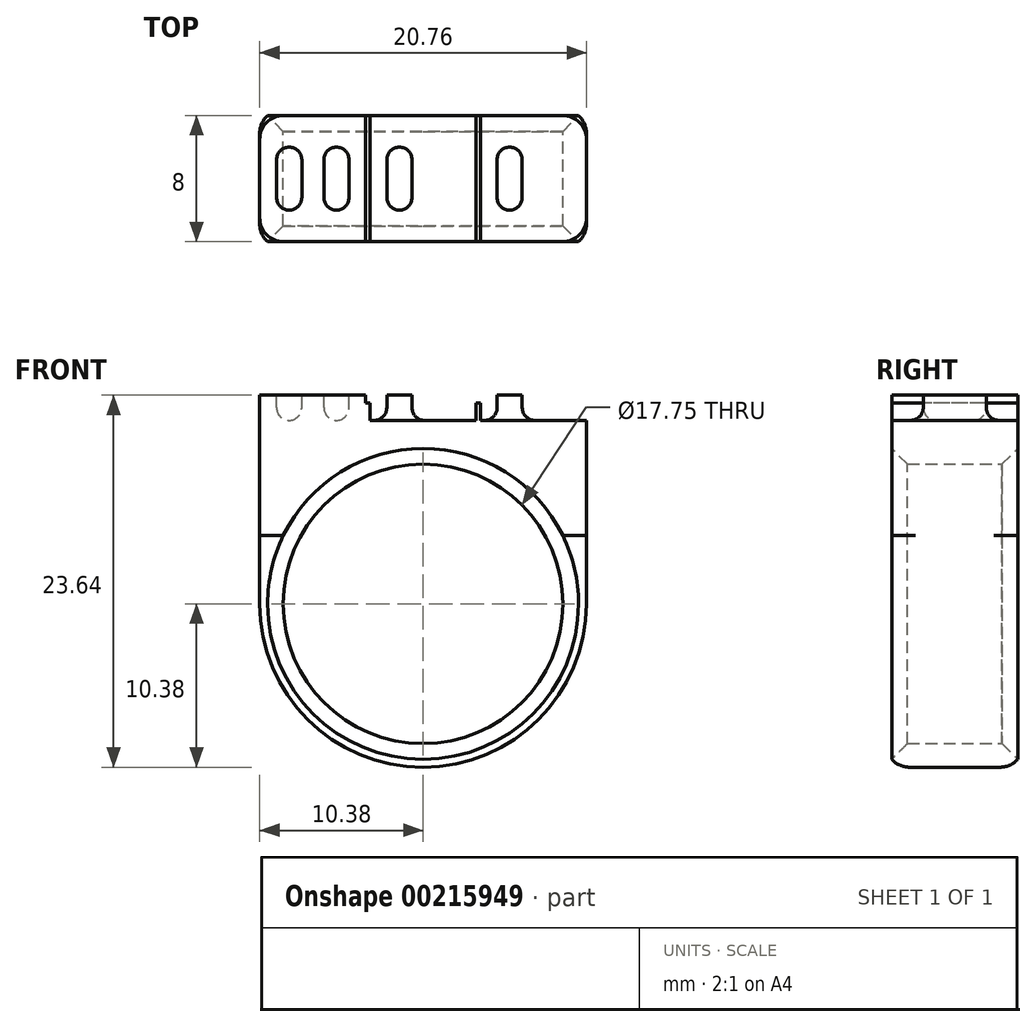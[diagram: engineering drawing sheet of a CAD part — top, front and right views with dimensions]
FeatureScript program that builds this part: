
annotation { "Feature Type Name" : "Feature", "Feature Type Description" : "" }
export const myFeature = defineFeature(function(context is Context, id is Id, definition is map)
    precondition{}
    {
        {
            var Q0;
            Q0=qCreatedBy(makeId("Front.planeOp"),FACE);
            var sketch = newSketch(context, id + "F0", { "sketchPlane" : qUnion([Q0])});
            skCircle(sketch, "E0", {"center": v(0, 0) * mm, "radius": 8.88 * mm});
            skCircle(sketch, "E1.0", {"center": v(0, 0) * mm, "radius": 10.38 * mm});
            skCircle(sketch, "E2.0", {"center": v(0, 0) * mm, "radius": 20.38 * mm});
            skLineSegment(sketch, "E3", {"start": v(10.38, 0) * mm, "end": v(10.38, 17.54) * mm});
            skLineSegment(sketch, "E4.MirrorCS", {"start": v(-10.38, 0) * mm, "end": v(-10.38, 17.54) * mm});
            skCircle(sketch, "E5.0", {"center": v(0, 0) * mm, "radius": 19.38 * mm});
            skLineSegment(sketch, "E6", {"start": v(-10.37, 13.26) * mm, "end": v(10.38, 13.26) * mm});
            skSolve(sketch);
        }
        {
            var Q0;
            Q0=makeQuery(id+"F0.imprint","IMPRINT",FACE,{"disambiguationData":[TD([[makeQuery(id+"F0.imprint","IMPRINT",EDGE,{"derivedFrom":sQuery(id+"F0.wireOp",EDGE,"E0")}),-1.0]])]});
            extrude(context, id + "F1", {"entities" : qUnion([Q0]), "depth" : 4 * mm, "hasSecondDirection" : true, "secondDirectionOppositeDirection" : true, "secondDirectionDepth" : 4 * mm});
        }
        {
            var Q0;
            Q0=makeQuery(id+"F1.opExtrude","CAP_EDGE",EDGE,{"disambiguationData":[OSD([sQuery(id+"F0.wireOp",EDGE,"E0")])],"isStart":false});
            var Q1;
            Q1=makeQuery(id+"F1.opExtrude","CAP_EDGE",EDGE,{"disambiguationData":[OSD([sQuery(id+"F0.wireOp",EDGE,"E0")])],"isStart":true});
            chamfer(context, id + "F2", {"entities" : qUnion([Q0, Q1]), "width" : 1 * mm, "tangentPropagation" : true});
        }
        {
            var Q0;
            {var subQ0=sQuery(id+"F0.wireOp",EDGE,"E3");var subQ1=sQuery(id+"F0.wireOp",EDGE,"E1.0");var subQ2=makeQuery(id+"F0.imprint","INTERSECT",VERTEX,{"derivedFrom":[subQ1,subQ0]});Q0=makeQuery(id+"F0.imprint","IMPRINT",FACE,{"disambiguationData":[TD([[makeQuery(id+"F0.imprint","IMPRINT",EDGE,{"disambiguationData":[TD([[subQ2,-1.0]])],"derivedFrom":subQ1}),-1.0]])]});}
            extrude(context, id + "F3", {"entities" : qUnion([Q0]), "operationType" : NewBodyOperationType.ADD, "depth" : 4 * mm, "hasSecondDirection" : true, "secondDirectionOppositeDirection" : true, "secondDirectionDepth" : 4 * mm});
        }
        {
            var Q0;
            {var subQ0=sQuery(id+"F0.wireOp",EDGE,"E3");var subQ1=sQuery(id+"F0.wireOp",EDGE,"E2.0");var subQ2=makeQuery(id+"F0.imprint","INTERSECT",VERTEX,{"derivedFrom":[subQ1,subQ0]});Q0=makeQuery(id+"F0.imprint","IMPRINT",FACE,{"disambiguationData":[TD([[makeQuery(id+"F0.imprint","IMPRINT",EDGE,{"disambiguationData":[TD([[subQ2,-1.0]])],"derivedFrom":subQ1}),1.0]])]});}
            extrude(context, id + "F4", {"entities" : qUnion([Q0]), "operationType" : NewBodyOperationType.REMOVE, "oppositeDirection" : true, "depth" : .5 * mm, "hasSecondDirection" : true, "secondDirectionOppositeDirection" : false, "secondDirectionDepth" : .5 * mm});
        }
        {
            var Q0;
            Q0=makeQuery(id+"F3.opExtrude","SWEPT_FACE",FACE,{"disambiguationData":[OSD([sQuery(id+"F0.wireOp",EDGE,"E6")])]});
            var sketch = newSketch(context, id + "F5", { "sketchPlane" : qUnion([Q0])});
            skLineSegment(sketch, "E7.bottom", {"start": v(1.5, 2) * mm, "end": v(1.5, 2) * mm});
            skLineSegment(sketch, "E7.top", {"start": v(1.5, -2) * mm, "end": v(1.5, -2) * mm});
            skLineSegment(sketch, "E7.left", {"start": v(0.7, 1.2) * mm, "end": v(0.7, -1.2) * mm});
            skLineSegment(sketch, "E7.right", {"start": v(2.3, 1.2) * mm, "end": v(2.3, -1.2) * mm});
            skLineSegment(sketch, "E8", {"start": v(0.7, 2) * mm, "end": v(2.3, -2) * mm, "construction": true});
            skLineSegment(sketch, "E9", {"start": v(2.3, 2) * mm, "end": v(0.7, -2) * mm, "construction": true});
            skPoint(sketch, "E10", {"position": v(1.5, 0) * mm});
            skPoint(sketch, "E11", {"position": v(3.5, 0) * mm});
            skLineSegment(sketch, "E12", {"start": v(3.5, 4) * mm, "end": v(3.5, 0) * mm, "construction": true});
            skLineSegment(sketch, "E13", {"start": v(3.5, -4) * mm, "end": v(3.5, 0) * mm, "construction": true});
            skPoint(sketch, "E14.visualSharp", {"position": v(0.7, 2) * mm});
            skArc(sketch, "E14.filletArc", {"start": v(1.5, 2) * mm, "mid": v(0.93, 1.77) * mm, "end": v(0.7, 1.2) * mm});
            skPoint(sketch, "E15.visualSharp", {"position": v(2.3, 2) * mm});
            skArc(sketch, "E15.filletArc", {"start": v(2.3, 1.2) * mm, "mid": v(2.07, 1.77) * mm, "end": v(1.5, 2) * mm});
            skPoint(sketch, "E16.visualSharp", {"position": v(2.3, -2) * mm});
            skArc(sketch, "E16.filletArc", {"start": v(1.5, -2) * mm, "mid": v(2.07, -1.77) * mm, "end": v(2.3, -1.2) * mm});
            skPoint(sketch, "E17.visualSharp", {"position": v(0.7, -2) * mm});
            skArc(sketch, "E17.filletArc", {"start": v(0.7, -1.2) * mm, "mid": v(0.93, -1.77) * mm, "end": v(1.5, -2) * mm});
            skPoint(sketch, "E18.MirrorP", {"position": v(4.7, -2) * mm});
            skLineSegment(sketch, "E19.MirrorCS", {"start": v(5.5, -2) * mm, "end": v(5.5, -2) * mm});
            skPoint(sketch, "E20.MirrorP", {"position": v(6.3, 2) * mm});
            skLineSegment(sketch, "E21.MirrorCS", {"start": v(5.5, 2) * mm, "end": v(5.5, 2) * mm});
            skPoint(sketch, "E22.MirrorP", {"position": v(6.3, -2) * mm});
            skArc(sketch, "E23.MirrorCS", {"start": v(6.3, -1.2) * mm, "mid": v(6.07, -1.77) * mm, "end": v(5.5, -2) * mm});
            skArc(sketch, "E24.MirrorCS", {"start": v(5.5, -2) * mm, "mid": v(4.93, -1.77) * mm, "end": v(4.7, -1.2) * mm});
            skPoint(sketch, "E25.MirrorP", {"position": v(5.5, 0) * mm});
            skLineSegment(sketch, "E26.MirrorCS", {"start": v(4.7, 2) * mm, "end": v(6.3, -2) * mm, "construction": true});
            skArc(sketch, "E27.MirrorCS", {"start": v(4.7, 1.2) * mm, "mid": v(4.93, 1.77) * mm, "end": v(5.5, 2) * mm});
            skPoint(sketch, "E28.MirrorP", {"position": v(4.7, 2) * mm});
            skLineSegment(sketch, "E29.MirrorCS", {"start": v(6.3, 2) * mm, "end": v(4.7, -2) * mm, "construction": true});
            skLineSegment(sketch, "E30.MirrorCS", {"start": v(6.3, 1.2) * mm, "end": v(6.3, -1.2) * mm});
            skLineSegment(sketch, "E31.MirrorCS", {"start": v(4.7, 1.2) * mm, "end": v(4.7, -1.2) * mm});
            skArc(sketch, "E32.MirrorCS", {"start": v(5.5, 2) * mm, "mid": v(6.07, 1.77) * mm, "end": v(6.3, 1.2) * mm});
            skPoint(sketch, "E33.MirrorP", {"position": v(-2.3, -2) * mm});
            skLineSegment(sketch, "E34.MirrorCS", {"start": v(-5.5, 2) * mm, "end": v(-5.5, 2) * mm});
            skLineSegment(sketch, "E35.MirrorCS", {"start": v(-4.7, 2) * mm, "end": v(-6.3, -2) * mm, "construction": true});
            skPoint(sketch, "E36.MirrorP", {"position": v(-0.7, -2) * mm});
            skArc(sketch, "E37.MirrorCS", {"start": v(-5.5, -2) * mm, "mid": v(-4.93, -1.77) * mm, "end": v(-4.7, -1.2) * mm});
            skArc(sketch, "E38.MirrorCS", {"start": v(-6.3, -1.2) * mm, "mid": v(-6.07, -1.77) * mm, "end": v(-5.5, -2) * mm});
            skArc(sketch, "E39.MirrorCS", {"start": v(-0.7, -1.2) * mm, "mid": v(-0.93, -1.77) * mm, "end": v(-1.5, -2) * mm});
            skArc(sketch, "E40.MirrorCS", {"start": v(-1.5, -2) * mm, "mid": v(-2.07, -1.77) * mm, "end": v(-2.3, -1.2) * mm});
            skArc(sketch, "E41.MirrorCS", {"start": v(-2.3, 1.2) * mm, "mid": v(-2.07, 1.77) * mm, "end": v(-1.5, 2) * mm});
            skArc(sketch, "E42.MirrorCS", {"start": v(-1.5, 2) * mm, "mid": v(-0.93, 1.77) * mm, "end": v(-0.7, 1.2) * mm});
            skLineSegment(sketch, "E43.MirrorCS", {"start": v(-2.3, 2) * mm, "end": v(-0.7, -2) * mm, "construction": true});
            skLineSegment(sketch, "E44.MirrorCS", {"start": v(-0.7, 2) * mm, "end": v(-2.3, -2) * mm, "construction": true});
            skArc(sketch, "E45.MirrorCS", {"start": v(-5.5, 2) * mm, "mid": v(-6.07, 1.77) * mm, "end": v(-6.3, 1.2) * mm});
            skPoint(sketch, "E46.MirrorP", {"position": v(-2.3, 2) * mm});
            skArc(sketch, "E47.MirrorCS", {"start": v(-4.7, 1.2) * mm, "mid": v(-4.93, 1.77) * mm, "end": v(-5.5, 2) * mm});
            skPoint(sketch, "E48.MirrorP", {"position": v(-0.7, 2) * mm});
            skLineSegment(sketch, "E49.MirrorCS", {"start": v(-2.3, 1.2) * mm, "end": v(-2.3, -1.2) * mm});
            skLineSegment(sketch, "E50.MirrorCS", {"start": v(-1.5, -2) * mm, "end": v(-1.5, -2) * mm});
            skPoint(sketch, "E51.MirrorP", {"position": v(-5.5, 0) * mm});
            skPoint(sketch, "E52.MirrorP", {"position": v(-6.3, 2) * mm});
            skPoint(sketch, "E53.MirrorP", {"position": v(-1.5, 0) * mm});
            skLineSegment(sketch, "E54.MirrorCS", {"start": v(-6.3, 2) * mm, "end": v(-4.7, -2) * mm, "construction": true});
            skLineSegment(sketch, "E55.MirrorCS", {"start": v(-0.7, 1.2) * mm, "end": v(-0.7, -1.2) * mm});
            skPoint(sketch, "E56.MirrorP", {"position": v(-6.3, -2) * mm});
            skPoint(sketch, "E57.MirrorP", {"position": v(-4.7, 2) * mm});
            skLineSegment(sketch, "E58.MirrorCS", {"start": v(-5.5, -2) * mm, "end": v(-5.5, -2) * mm});
            skPoint(sketch, "E59.MirrorP", {"position": v(-3.5, 0) * mm});
            skLineSegment(sketch, "E60.MirrorCS", {"start": v(-1.5, 2) * mm, "end": v(-1.5, 2) * mm});
            skLineSegment(sketch, "E61.MirrorCS", {"start": v(-4.7, 1.2) * mm, "end": v(-4.7, -1.2) * mm});
            skLineSegment(sketch, "E62.MirrorCS", {"start": v(-6.3, 1.2) * mm, "end": v(-6.3, -1.2) * mm});
            skPoint(sketch, "E63.MirrorP", {"position": v(-4.7, -2) * mm});
            skPoint(sketch, "E64", {"position": v(-10.38, 4) * mm});
            skPoint(sketch, "E65", {"position": v(10.38, 4) * mm});
            skPoint(sketch, "E66", {"position": v(7, 0) * mm});
            skLineSegment(sketch, "E67", {"start": v(7, -4) * mm, "end": v(7, 0) * mm, "construction": true});
            skLineSegment(sketch, "E68.MirrorCS", {"start": v(8.5, -2) * mm, "end": v(8.5, -2) * mm});
            skLineSegment(sketch, "E69.MirrorCS", {"start": v(8.5, 2) * mm, "end": v(8.5, 2) * mm});
            skPoint(sketch, "E70.MirrorP", {"position": v(9.3, 2) * mm});
            skPoint(sketch, "E71.MirrorP", {"position": v(9.3, -2) * mm});
            skLineSegment(sketch, "E72.MirrorCS", {"start": v(9.3, 1.2) * mm, "end": v(9.3, -1.2) * mm});
            skPoint(sketch, "E73.MirrorP", {"position": v(8.5, 0) * mm});
            skArc(sketch, "E74.MirrorCS", {"start": v(9.3, 1.2) * mm, "mid": v(9.07, 1.77) * mm, "end": v(8.5, 2) * mm});
            skPoint(sketch, "E75.MirrorP", {"position": v(7.7, 2) * mm});
            skArc(sketch, "E76.MirrorCS", {"start": v(8.5, 2) * mm, "mid": v(7.93, 1.77) * mm, "end": v(7.7, 1.2) * mm});
            skLineSegment(sketch, "E77.MirrorCS", {"start": v(9.3, 2) * mm, "end": v(7.7, -2) * mm, "construction": true});
            skLineSegment(sketch, "E78.MirrorCS", {"start": v(7.7, 1.2) * mm, "end": v(7.7, -1.2) * mm});
            skArc(sketch, "E79.MirrorCS", {"start": v(7.7, -1.2) * mm, "mid": v(7.93, -1.77) * mm, "end": v(8.5, -2) * mm});
            skArc(sketch, "E80.MirrorCS", {"start": v(8.5, -2) * mm, "mid": v(9.07, -1.77) * mm, "end": v(9.3, -1.2) * mm});
            skPoint(sketch, "E81.MirrorP", {"position": v(7.7, -2) * mm});
            skLineSegment(sketch, "E82.MirrorCS", {"start": v(7.7, 2) * mm, "end": v(9.3, -2) * mm, "construction": true});
            skLineSegment(sketch, "E83.MirrorCS", {"start": v(-8.5, 2) * mm, "end": v(-8.5, 2) * mm});
            skLineSegment(sketch, "E84.MirrorCS", {"start": v(-8.5, -2) * mm, "end": v(-8.5, -2) * mm});
            skLineSegment(sketch, "E85.MirrorCS", {"start": v(-9.3, 2) * mm, "end": v(-7.7, -2) * mm, "construction": true});
            skPoint(sketch, "E86.MirrorP", {"position": v(-7.7, 2) * mm});
            skLineSegment(sketch, "E87.MirrorCS", {"start": v(-7.7, 1.2) * mm, "end": v(-7.7, -1.2) * mm});
            skLineSegment(sketch, "E88.MirrorCS", {"start": v(-7.7, 2) * mm, "end": v(-9.3, -2) * mm, "construction": true});
            skLineSegment(sketch, "E89.MirrorCS", {"start": v(-9.3, 1.2) * mm, "end": v(-9.3, -1.2) * mm});
            skPoint(sketch, "E90.MirrorP", {"position": v(-8.5, 0) * mm});
            skArc(sketch, "E91.MirrorCS", {"start": v(-9.3, 1.2) * mm, "mid": v(-9.07, 1.77) * mm, "end": v(-8.5, 2) * mm});
            skArc(sketch, "E92.MirrorCS", {"start": v(-7.7, -1.2) * mm, "mid": v(-7.93, -1.77) * mm, "end": v(-8.5, -2) * mm});
            skArc(sketch, "E93.MirrorCS", {"start": v(-8.5, 2) * mm, "mid": v(-7.93, 1.77) * mm, "end": v(-7.7, 1.2) * mm});
            skPoint(sketch, "E94.MirrorP", {"position": v(-9.3, 2) * mm});
            skArc(sketch, "E95.MirrorCS", {"start": v(-8.5, -2) * mm, "mid": v(-9.07, -1.77) * mm, "end": v(-9.3, -1.2) * mm});
            skPoint(sketch, "E96.MirrorP", {"position": v(-9.3, -2) * mm});
            skPoint(sketch, "E97.MirrorP", {"position": v(-7.7, -2) * mm});
            skLineSegment(sketch, "E98", {"start": v(3.35, 4) * mm, "end": v(3.35, -4) * mm});
            skLineSegment(sketch, "E99.MirrorCS", {"start": v(3.65, 4) * mm, "end": v(3.65, -4) * mm});
            skLineSegment(sketch, "E100", {"start": v(3.35, 4) * mm, "end": v(3.65, 4) * mm});
            skLineSegment(sketch, "E101", {"start": v(3.35, -4) * mm, "end": v(3.65, -4) * mm});
            skLineSegment(sketch, "E102.MirrorCS", {"start": v(-3.35, 4) * mm, "end": v(-3.65, 4) * mm});
            skLineSegment(sketch, "E103.MirrorCS", {"start": v(-3.35, -4) * mm, "end": v(-3.65, -4) * mm});
            skLineSegment(sketch, "E104.MirrorCS", {"start": v(-3.35, 4) * mm, "end": v(-3.35, -4) * mm});
            skLineSegment(sketch, "E105.MirrorCS", {"start": v(-3.65, 4) * mm, "end": v(-3.65, -4) * mm});
            skLineSegment(sketch, "E106.MirrorCS", {"start": v(-3.5, -4) * mm, "end": v(-3.5, 0) * mm, "construction": true});
            skLineSegment(sketch, "E107.MirrorCS", {"start": v(-3.5, 4) * mm, "end": v(-3.5, 0) * mm, "construction": true});
            skSolve(sketch);
        }
        {
            var Q0;
            Q0=makeQuery(id+"F5.imprint","IMPRINT",FACE,{"disambiguationData":[TD([[makeQuery(id+"F5.imprint","IMPRINT",EDGE,{"derivedFrom":sQuery(id+"F5.wireOp",EDGE,"E72.MirrorCS")}),-1.0]])]});
            var Q1;
            Q1=makeQuery(id+"F5.imprint","IMPRINT",FACE,{"disambiguationData":[TD([[makeQuery(id+"F5.imprint","IMPRINT",EDGE,{"derivedFrom":sQuery(id+"F5.wireOp",EDGE,"E23.MirrorCS")}),-1.0]])]});
            var Q2;
            Q2=makeQuery(id+"F5.imprint","IMPRINT",FACE,{"disambiguationData":[TD([[makeQuery(id+"F5.imprint","IMPRINT",EDGE,{"derivedFrom":sQuery(id+"F5.wireOp",EDGE,"E7.left")}),1.0]])]});
            var Q3;
            Q3=makeQuery(id+"F5.imprint","IMPRINT",FACE,{"disambiguationData":[TD([[makeQuery(id+"F5.imprint","IMPRINT",EDGE,{"derivedFrom":sQuery(id+"F5.wireOp",EDGE,"E39.MirrorCS")}),-1.0]])]});
            var Q4;
            Q4=makeQuery(id+"F5.imprint","IMPRINT",FACE,{"disambiguationData":[TD([[makeQuery(id+"F5.imprint","IMPRINT",EDGE,{"derivedFrom":sQuery(id+"F5.wireOp",EDGE,"E37.MirrorCS")}),1.0]])]});
            var Q5;
            Q5=makeQuery(id+"F5.imprint","IMPRINT",FACE,{"disambiguationData":[TD([[makeQuery(id+"F5.imprint","IMPRINT",EDGE,{"derivedFrom":sQuery(id+"F5.wireOp",EDGE,"E87.MirrorCS")}),-1.0]])]});
            extrude(context, id + "F6", {"entities" : qUnion([Q0, Q1, Q2, Q3, Q4, Q5]), "operationType" : NewBodyOperationType.REMOVE, "oppositeDirection" : true, "depth" : 1.6 * mm});
        }
        {
            var Q0;
            Q0=makeQuery(id+"F6.boolean.opBoolean","COPY",EDGE,{"derivedFrom":makeQuery(id+"F6.opExtrude","CAP_EDGE",EDGE,{"disambiguationData":[OSD([sQuery(id+"F5.wireOp",EDGE,"E74.MirrorCS"),sQuery(id+"F5.wireOp",EDGE,"E76.MirrorCS")])],"isStart":false})});
            var Q1;
            Q1=makeQuery(id+"F6.boolean.opBoolean","COPY",EDGE,{"derivedFrom":makeQuery(id+"F6.opExtrude","CAP_EDGE",EDGE,{"disambiguationData":[OSD([sQuery(id+"F5.wireOp",EDGE,"E27.MirrorCS"),sQuery(id+"F5.wireOp",EDGE,"E32.MirrorCS")])],"isStart":false})});
            var Q2;
            Q2=makeQuery(id+"F6.boolean.opBoolean","COPY",EDGE,{"derivedFrom":makeQuery(id+"F6.opExtrude","CAP_EDGE",EDGE,{"disambiguationData":[OSD([sQuery(id+"F5.wireOp",EDGE,"E14.filletArc"),sQuery(id+"F5.wireOp",EDGE,"E15.filletArc")])],"isStart":false})});
            var Q3;
            Q3=makeQuery(id+"F6.boolean.opBoolean","COPY",EDGE,{"derivedFrom":makeQuery(id+"F6.opExtrude","CAP_EDGE",EDGE,{"disambiguationData":[OSD([sQuery(id+"F5.wireOp",EDGE,"E41.MirrorCS"),sQuery(id+"F5.wireOp",EDGE,"E42.MirrorCS")])],"isStart":false})});
            var Q4;
            Q4=makeQuery(id+"F6.boolean.opBoolean","COPY",EDGE,{"derivedFrom":makeQuery(id+"F6.opExtrude","CAP_EDGE",EDGE,{"disambiguationData":[OSD([sQuery(id+"F5.wireOp",EDGE,"E45.MirrorCS"),sQuery(id+"F5.wireOp",EDGE,"E47.MirrorCS")])],"isStart":false})});
            var Q5;
            Q5=makeQuery(id+"F6.boolean.opBoolean","COPY",EDGE,{"derivedFrom":makeQuery(id+"F6.opExtrude","CAP_EDGE",EDGE,{"disambiguationData":[OSD([sQuery(id+"F5.wireOp",EDGE,"E91.MirrorCS"),sQuery(id+"F5.wireOp",EDGE,"E93.MirrorCS")])],"isStart":false})});
            fillet(context, id + "F7", {"entities" : qUnion([Q0, Q1, Q2, Q3, Q4, Q5]), "radius" : (1.6 / 2) * mm, "tangentPropagation" : true, "allowEdgeOverflow" : false});
        }
        {
            var Q0;
            Q0=makeQuery(id+"F3.opExtrude","CAP_EDGE",EDGE,{"disambiguationData":[OSD([sQuery(id+"F0.wireOp",EDGE,"E3")])],"isStart":true});
            var Q1;
            Q1=makeQuery(id+"F3.opExtrude","CAP_EDGE",EDGE,{"disambiguationData":[OSD([sQuery(id+"F0.wireOp",EDGE,"E4.MirrorCS")])],"isStart":false});
            fillet(context, id + "F8", {"entities" : qUnion([Q0, Q1]), "radius" : 1.5 * mm, "tangentPropagation" : true, "allowEdgeOverflow" : false});
        }
        {
            var Q0;
            Q0=makeQuery(id+"F5.imprint","IMPRINT",FACE,{"disambiguationData":[TD([[makeQuery(id+"F5.imprint","IMPRINT",EDGE,{"derivedFrom":sQuery(id+"F5.wireOp",EDGE,"E98")}),1.0]])]});
            var Q1;
            Q1=makeQuery(id+"F5.imprint","IMPRINT",FACE,{"disambiguationData":[TD([[makeQuery(id+"F5.imprint","IMPRINT",EDGE,{"derivedFrom":sQuery(id+"F5.wireOp",EDGE,"E102.MirrorCS")}),-1.0]])]});
            extrude(context, id + "F9", {"entities" : qUnion([Q0, Q1]), "operationType" : NewBodyOperationType.REMOVE, "oppositeDirection" : true, "depth" : .5 * mm});
        }
    });
